# Revit family: Strebe 45° lang
name_source: partatom
category: HLS-Bauteile
revit_build: Autodesk Revit 2017 (Build: 20190507_1515(x64)
units: mm (PartAtom-declared; Revit-internal decimal feet)

## family parameters
Arbeitsebenenbasiert = Ja
Beim Laden mit Abzugskörper schneiden = Nein
Bemaßung runder Anschluss = Durchmesser verwenden
Gemeinsam genutzt = Ja
Immer vertikal = Nein
Raumberechnungspunkt = Nein
Teiletyp = Normal

## types (1)
- Strebe 45° lang
    Artikelnummer = 0815102
    Breite Material = 45 mm
    EAN = 4250928449009
    Fabrikat = MEFA
    Firma = MEFA Befestigungs- und Montagesysteme GmbH
    Gewicht = 2.07 kg
    Gewicht pro Bauteil = 2.07 kg
    Konsolentyp = 45
    Kurztext1 = Strebe 45°
    Kurztext2 = L= 616 mm für Konsole 45
    Langloch = 20 x 13 mm
    Länge = 616 mm  [stored 2.021 ft]
    Material = Stahl
    Materialname = S235
    Mengeneinheit = St
    Oberflaeche = galvanisch verzinkt
    Vorgabe-Ansicht = 1219 mm
    vpe = 4 St

note: [stored X ft] marks values corroborated as IEEE doubles in the binary element streams (Revit-internal decimal feet)
